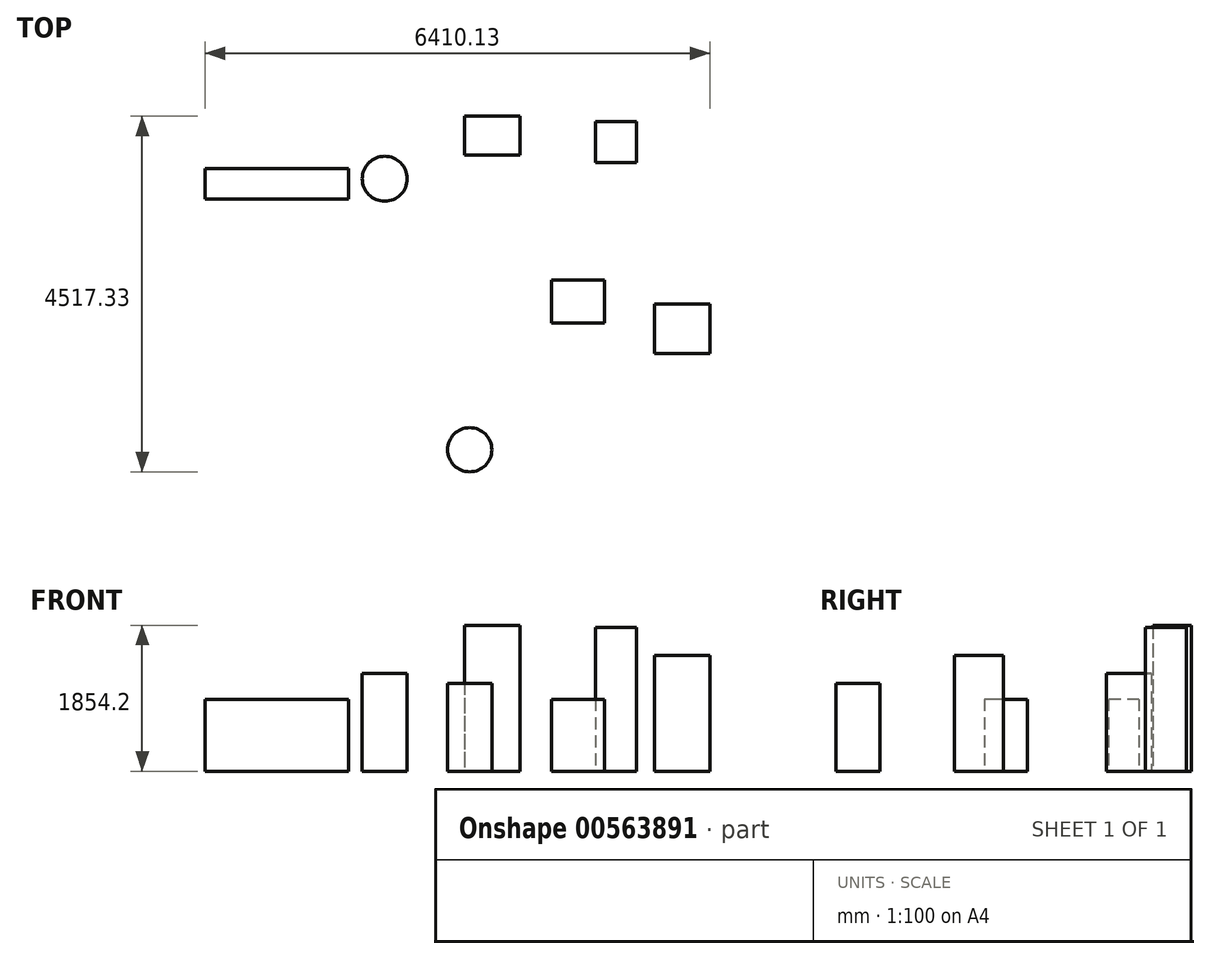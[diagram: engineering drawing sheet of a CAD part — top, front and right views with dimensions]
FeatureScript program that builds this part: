
annotation { "Feature Type Name" : "Feature", "Feature Type Description" : "" }
export const myFeature = defineFeature(function(context is Context, id is Id, definition is map)
    precondition{}
    {
        {
            var Q0;
            Q0=qCreatedBy(makeId("Top.planeOp"),FACE);
            var sketch = newSketch(context, id + "F0", { "sketchPlane" : qUnion([Q0])});
            skLineSegment(sketch, "E0.bottom", {"start": v(2745.58, -90.88) * mm, "end": v(1826.41, -90.88) * mm});
            skLineSegment(sketch, "E0.top", {"start": v(2745.58, -630.2) * mm, "end": v(1826.41, -630.2) * mm});
            skLineSegment(sketch, "E0.left", {"start": v(2745.58, -90.88) * mm, "end": v(2745.58, -630.2) * mm});
            skLineSegment(sketch, "E0.right", {"start": v(1826.41, -90.88) * mm, "end": v(1826.41, -630.2) * mm});
            skSolve(sketch);
        }
        {
            var Q0;
            Q0 = qSketchRegion(id + "F0", true);
            extrude(context, id + "F1", {"entities" : qUnion([Q0]), "depth" : 25.4 * mm, "offsetDistance" : 25.4 * mm});
        }
        {
            var Q0;
            Q0=qCreatedBy(makeId("Top.planeOp"),FACE);
            var sketch = newSketch(context, id + "F2", { "sketchPlane" : qUnion([Q0])});
            skLineSegment(sketch, "E1.bottom", {"start": v(590.7, 1592.39) * mm, "end": v(1291.63, 1592.39) * mm});
            skLineSegment(sketch, "E1.top", {"start": v(590.7, 2083.42) * mm, "end": v(1291.63, 2083.42) * mm});
            skLineSegment(sketch, "E1.left", {"start": v(590.7, 1592.39) * mm, "end": v(590.7, 2083.42) * mm});
            skLineSegment(sketch, "E1.right", {"start": v(1291.63, 1592.39) * mm, "end": v(1291.63, 2083.42) * mm});
            skSolve(sketch);
        }
        {
            var Q0;
            Q0 = qSketchRegion(id + "F2", true);
            extrude(context, id + "F3", {"entities" : qUnion([Q0]), "depth" : 1854.2 * mm, "offsetDistance" : 25.4 * mm});
        }
        {
            var Q0;
            Q0=makeQuery(id+"F1.opExtrude","SWEPT_BODY",BODY,{"disambiguationData":[OSD([sQuery(id+"F0.wireOp",EDGE,"E0.bottom"),sQuery(id+"F0.wireOp",EDGE,"E0.top"),sQuery(id+"F0.wireOp",EDGE,"E0.left"),sQuery(id+"F0.wireOp",EDGE,"E0.right")])]});
            deleteBodies(context, id + "F4", {"entities" : qUnion([Q0])});
        }
        {
            var Q0;
            Q0=qCreatedBy(makeId("Top.planeOp"),FACE);
            var sketch = newSketch(context, id + "F5", { "sketchPlane" : qUnion([Q0])});
            skLineSegment(sketch, "E2.bottom", {"start": v(1691.93, 0) * mm, "end": v(2364.03, 0) * mm});
            skLineSegment(sketch, "E2.top", {"start": v(1691.93, -544.31) * mm, "end": v(2364.03, -544.31) * mm});
            skLineSegment(sketch, "E2.left", {"start": v(1691.93, 0) * mm, "end": v(1691.93, -544.31) * mm});
            skLineSegment(sketch, "E2.right", {"start": v(2364.03, 0) * mm, "end": v(2364.03, -544.31) * mm});
            skSolve(sketch);
        }
        {
            var Q0;
            Q0 = qSketchRegion(id + "F5", true);
            extrude(context, id + "F6", {"entities" : qUnion([Q0]), "depth" : 914.4 * mm, "offsetDistance" : 25.4 * mm});
        }
        {
            var Q0;
            Q0=qCreatedBy(makeId("Top.planeOp"),FACE);
            var sketch = newSketch(context, id + "F7", { "sketchPlane" : qUnion([Q0])});
            skCircle(sketch, "E3", {"center": v(-395.41, 1610.26) * mm, "radius": 178.74 * mm});
            skSolve(sketch);
        }
        {
            var Q0;
            Q0 = qSketchRegion(id + "F7", true);
            extrude(context, id + "F8", {"entities" : qUnion([Q0]), "depth" : 939.8 * mm, "offsetDistance" : 25.4 * mm});
        }
        {
            var Q0;
            Q0=qCreatedBy(makeId("Top.planeOp"),FACE);
            var sketch = newSketch(context, id + "F9", { "sketchPlane" : qUnion([Q0])});
            skLineSegment(sketch, "E4.bottom", {"start": v(2249.65, 1497.86) * mm, "end": v(2770.73, 1497.86) * mm});
            skLineSegment(sketch, "E4.top", {"start": v(2249.65, 2016.54) * mm, "end": v(2770.73, 2016.54) * mm});
            skLineSegment(sketch, "E4.left", {"start": v(2249.65, 1497.86) * mm, "end": v(2249.65, 2016.54) * mm});
            skLineSegment(sketch, "E4.right", {"start": v(2770.73, 1497.86) * mm, "end": v(2770.73, 2016.54) * mm});
            skSolve(sketch);
        }
        {
            var Q0;
            Q0 = qSketchRegion(id + "F9", true);
            extrude(context, id + "F10", {"entities" : qUnion([Q0]), "depth" : 1828.8 * mm, "offsetDistance" : 25.4 * mm});
        }
        {
            var Q0;
            Q0=qCreatedBy(makeId("Top.planeOp"),FACE);
            var sketch = newSketch(context, id + "F11", { "sketchPlane" : qUnion([Q0])});
            skLineSegment(sketch, "E5.bottom", {"start": v(3003.8, -927.74) * mm, "end": v(3704.6, -927.74) * mm});
            skLineSegment(sketch, "E5.top", {"start": v(3003.8, -305.29) * mm, "end": v(3704.6, -305.29) * mm});
            skLineSegment(sketch, "E5.left", {"start": v(3003.8, -927.74) * mm, "end": v(3003.8, -305.29) * mm});
            skLineSegment(sketch, "E5.right", {"start": v(3704.6, -927.74) * mm, "end": v(3704.6, -305.29) * mm});
            skSolve(sketch);
        }
        {
            var Q0;
            Q0=makeQuery(id+"F11.imprint","IMPRINT",FACE,{"disambiguationData":[TD([[makeQuery(id+"F11.imprint","IMPRINT",EDGE,{"derivedFrom":sQuery(id+"F11.wireOp",EDGE,"E5.bottom")}),1.0]])]});
            extrude(context, id + "F12", {"entities" : qUnion([Q0]), "depth" : 1473.2 * mm, "offsetDistance" : 25.4 * mm});
        }
        {
            var Q0;
            Q0=qCreatedBy(makeId("Top.planeOp"),FACE);
            var sketch = newSketch(context, id + "F13", { "sketchPlane" : qUnion([Q0])});
            skCircle(sketch, "E6", {"center": v(-951.28, -655.18) * mm, "radius": 135.46 * mm});
            skSolve(sketch);
        }
        {
            var Q0;
            Q0 = qSketchRegion(id + "F13", true);
            extrude(context, id + "F14", {"entities" : qUnion([Q0]), "depth" : 1016 * mm, "offsetDistance" : 25.4 * mm});
        }
        {
            var Q0;
            Q0=qCreatedBy(makeId("Top.planeOp"),FACE);
            var sketch = newSketch(context, id + "F15", { "sketchPlane" : qUnion([Q0])});
            skCircle(sketch, "E7", {"center": v(654.4, -2153.45) * mm, "radius": 280.46 * mm});
            skSolve(sketch);
        }
        {
            var Q0;
            Q0 = qSketchRegion(id + "F15", true);
            extrude(context, id + "F16", {"entities" : qUnion([Q0]), "depth" : 1117.6 * mm, "offsetDistance" : 25.4 * mm});
        }
        {
            var Q0;
            Q0=makeQuery(id+"F14.opExtrude","SWEPT_BODY",BODY,{"disambiguationData":[OSD([sQuery(id+"F13.wireOp",EDGE,"E6")])]});
            deleteBodies(context, id + "F17", {"entities" : qUnion([Q0])});
        }
        {
            var Q0;
            Q0=makeQuery(id+"F8.opExtrude","SWEPT_BODY",BODY,{"disambiguationData":[OSD([sQuery(id+"F7.wireOp",EDGE,"E3")])]});
            deleteBodies(context, id + "F18", {"entities" : qUnion([Q0])});
        }
        {
            var Q0;
            Q0=qCreatedBy(makeId("Top.planeOp"),FACE);
            var sketch = newSketch(context, id + "F19", { "sketchPlane" : qUnion([Q0])});
            skCircle(sketch, "E8", {"center": v(-425.63, 1289.38) * mm, "radius": 286.04 * mm});
            skSolve(sketch);
        }
        {
            var Q0;
            Q0 = qSketchRegion(id + "F19", true);
            extrude(context, id + "F20", {"entities" : qUnion([Q0]), "depth" : 1244.6 * mm, "offsetDistance" : 25.4 * mm});
        }
        {
            var Q0;
            Q0=qCreatedBy(makeId("Top.planeOp"),FACE);
            var sketch = newSketch(context, id + "F21", { "sketchPlane" : qUnion([Q0])});
            skLineSegment(sketch, "E9.bottom", {"start": v(-2705.53, 1417.84) * mm, "end": v(-884.8, 1417.84) * mm});
            skLineSegment(sketch, "E9.top", {"start": v(-2705.53, 1030.71) * mm, "end": v(-884.8, 1030.71) * mm});
            skLineSegment(sketch, "E9.left", {"start": v(-2705.53, 1417.84) * mm, "end": v(-2705.53, 1030.71) * mm});
            skLineSegment(sketch, "E9.right", {"start": v(-884.8, 1417.84) * mm, "end": v(-884.8, 1030.71) * mm});
            skSolve(sketch);
        }
        {
            var Q0;
            Q0 = qSketchRegion(id + "F21", true);
            extrude(context, id + "F22", {"entities" : qUnion([Q0]), "depth" : 914.4 * mm, "offsetDistance" : 25.4 * mm});
        }
    });
